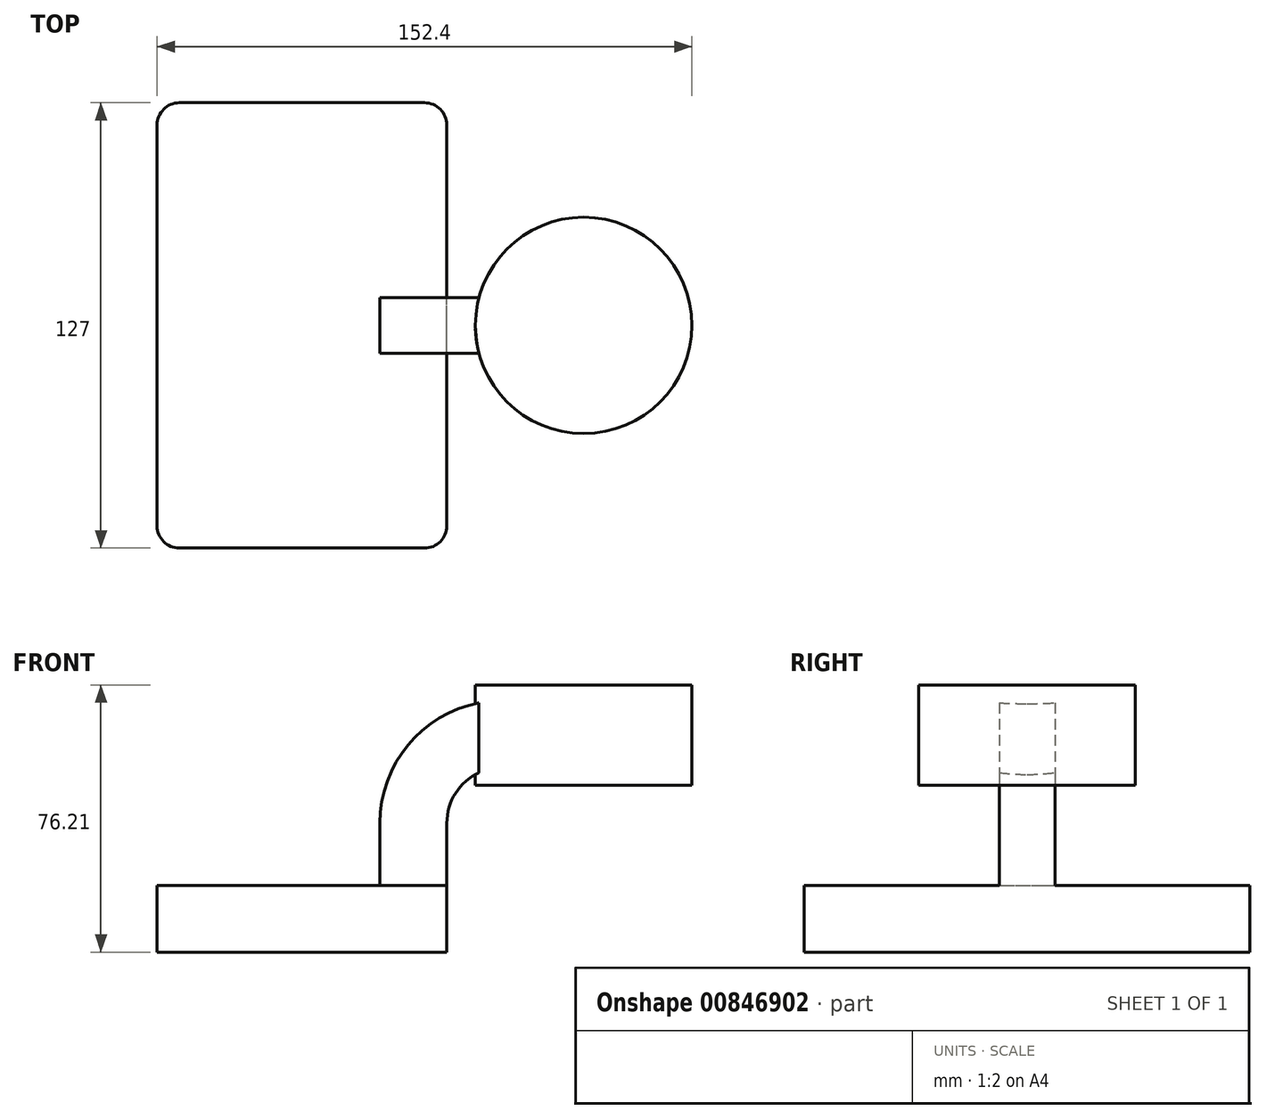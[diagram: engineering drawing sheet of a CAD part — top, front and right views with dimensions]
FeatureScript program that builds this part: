
annotation { "Feature Type Name" : "Feature", "Feature Type Description" : "" }
export const myFeature = defineFeature(function(context is Context, id is Id, definition is map)
    precondition{}
    {
        {
            var Q0;
            Q0=qCreatedBy(makeId("Front.planeOp"),FACE);
            var sketch = newSketch(context, id + "F0", { "sketchPlane" : qUnion([Q0])});
            skLineSegment(sketch, "E0.bottom", {"start": v(41.27, 9.53) * mm, "end": v(-41.28, 9.53) * mm});
            skLineSegment(sketch, "E0.top", {"start": v(41.28, -9.52) * mm, "end": v(-41.27, -9.52) * mm});
            skLineSegment(sketch, "E0.left", {"start": v(41.28, 9.53) * mm, "end": v(41.28, -9.52) * mm});
            skLineSegment(sketch, "E0.right", {"start": v(-41.28, 9.53) * mm, "end": v(-41.27, -9.52) * mm});
            skPoint(sketch, "E0.middle", {"position": v(0, 0) * mm});
            skLineSegment(sketch, "E1.bottom", {"start": v(60.33, 38.1) * mm, "end": v(111.13, 38.1) * mm});
            skLineSegment(sketch, "E1.top", {"start": v(60.33, 66.68) * mm, "end": v(111.13, 66.68) * mm});
            skLineSegment(sketch, "E1.left", {"start": v(60.33, 38.1) * mm, "end": v(60.33, 66.68) * mm});
            skLineSegment(sketch, "E1.right", {"start": v(111.13, 38.1) * mm, "end": v(111.13, 66.68) * mm});
            skPoint(sketch, "E1.middle", {"position": v(85.73, 52.39) * mm});
            skLineSegment(sketch, "E2.bottom", {"start": v(41.28, 27.26) * mm, "end": v(41.28, 27.26) * mm});
            skLineSegment(sketch, "E2.top", {"start": v(41.27, -8.2) * mm, "end": v(41.28, -8.2) * mm});
            skPoint(sketch, "E2.middle", {"position": v(41.27, 9.53) * mm});
            skArc(sketch, "E3", {"start": v(41.27, 27.26) * mm, "mid": v(45.92, 38.48) * mm, "end": v(57.15, 43.13) * mm});
            skLineSegment(sketch, "E4", {"start": v(57.15, 43.13) * mm, "end": v(79.8, 43.13) * mm});
            skLineSegment(sketch, "E5", {"start": v(41.27, 9.53) * mm, "end": v(41.27, 27.26) * mm});
            skLineSegment(sketch, "E6.0", {"start": v(57.15, 62.18) * mm, "end": v(79.8, 62.18) * mm});
            skArc(sketch, "E6.1", {"start": v(22.22, 27.26) * mm, "mid": v(32.45, 51.95) * mm, "end": v(57.15, 62.18) * mm});
            skLineSegment(sketch, "E6.2", {"start": v(22.23, 9.53) * mm, "end": v(22.22, 27.26) * mm});
            skLineSegment(sketch, "E7", {"start": v(80.27, 38.1) * mm, "end": v(80.27, 66.68) * mm});
            skFitSpline(sketch, "E8", {"points": [v(-41.28, 9.52) * mm, v(57.15, 62.18) * mm], "startDerivative": vector(74.42, 20.64) * mm, "endDerivative": vector(254.34, -45.9) * mm});
            skSolve(sketch);
        }
        {
            var Q0;
            Q0=makeQuery(id+"F0.imprint","IMPRINT",FACE,{"disambiguationData":[TD([[makeQuery(id+"F0.imprint","IMPRINT",EDGE,{"derivedFrom":sQuery(id+"F0.wireOp",EDGE,"E0.top")}),-1.0]])]});
            extrude(context, id + "F1", {"entities" : qUnion([Q0]), "endBound" : BoundingType.SYMMETRIC, "depth" : 127 * mm, "offsetDistance" : 25.4 * mm});
        }
        {
            var Q0;
            {var subQ6=sQuery(id+"F0.wireOp",EDGE,"E7");Q0=makeQuery(id+"F0.imprint","IMPRINT",FACE,{"disambiguationData":[TD([[makeQuery(id+"F0.imprint","IMPRINT",EDGE,{"derivedFrom":subQ6}),1.0]])]});}
            var Q1;
            {var subQ1=sQuery(id+"F0.wireOp",EDGE,"E3");Q1=makeQuery(id+"F0.imprint","IMPRINT",FACE,{"disambiguationData":[TD([[makeQuery(id+"F0.imprint","IMPRINT",EDGE,{"derivedFrom":subQ1}),1.0]])]});}
            extrude(context, id + "F2", {"entities" : qUnion([Q0, Q1]), "operationType" : NewBodyOperationType.ADD, "endBound" : BoundingType.SYMMETRIC, "depth" : 25.4 * mm, "offsetDistance" : 25.4 * mm});
        }
        {
            var Q0;
            Q0=makeQuery(id+"F0.imprint","IMPRINT",FACE,{"disambiguationData":[TD([[makeQuery(id+"F0.imprint","IMPRINT",EDGE,{"derivedFrom":sQuery(id+"F0.wireOp",EDGE,"E6.1")}),1.0]])]});
            extrude(context, id + "F3", {"entities" : qUnion([Q0]), "operationType" : NewBodyOperationType.ADD, "endBound" : BoundingType.SYMMETRIC, "depth" : 15.88 * mm, "offsetDistance" : 25.4 * mm});
        }
        {
            var Q0;
            {var subQ0=sQuery(id+"F0.wireOp",EDGE,"E1.right");Q0=makeQuery(id+"F0.imprint","IMPRINT",FACE,{"disambiguationData":[TD([[makeQuery(id+"F0.imprint","IMPRINT",EDGE,{"derivedFrom":subQ0}),1.0]])]});}
            var Q1;
            Q1=sQuery(id+"F0.wireOp",EDGE,"E7");
            revolve(context, id + "F4", {"operationType" : NewBodyOperationType.ADD, "surfaceOperationType" : NewSurfaceOperationType.NEW, "entities" : qUnion([Q0]), "axis" : qUnion([Q1]), "revolveType" : RevolveType.FULL});
        }
        {
            var Q0;
            Q0=makeQuery(id+"F1.opExtrude","CAP_EDGE",EDGE,{"disambiguationData":[OSD([sQuery(id+"F0.wireOp",EDGE,"E0.right")])],"isStart":false});
            var Q1;
            Q1=makeQuery(id+"F1.opExtrude","CAP_EDGE",EDGE,{"disambiguationData":[OSD([sQuery(id+"F0.wireOp",EDGE,"E0.left")])],"isStart":false});
            var Q2;
            Q2=makeQuery(id+"F1.opExtrude","CAP_EDGE",EDGE,{"disambiguationData":[OSD([sQuery(id+"F0.wireOp",EDGE,"E0.left")])],"isStart":true});
            var Q3;
            Q3=makeQuery(id+"F1.opExtrude","CAP_EDGE",EDGE,{"disambiguationData":[OSD([sQuery(id+"F0.wireOp",EDGE,"E0.right")])],"isStart":true});
            fillet(context, id + "F5", {"entities" : qUnion([Q0, Q1, Q2, Q3]), "radius" : 6.35 * mm, "tangentPropagation" : true, "allowEdgeOverflow" : false});
        }
    });
